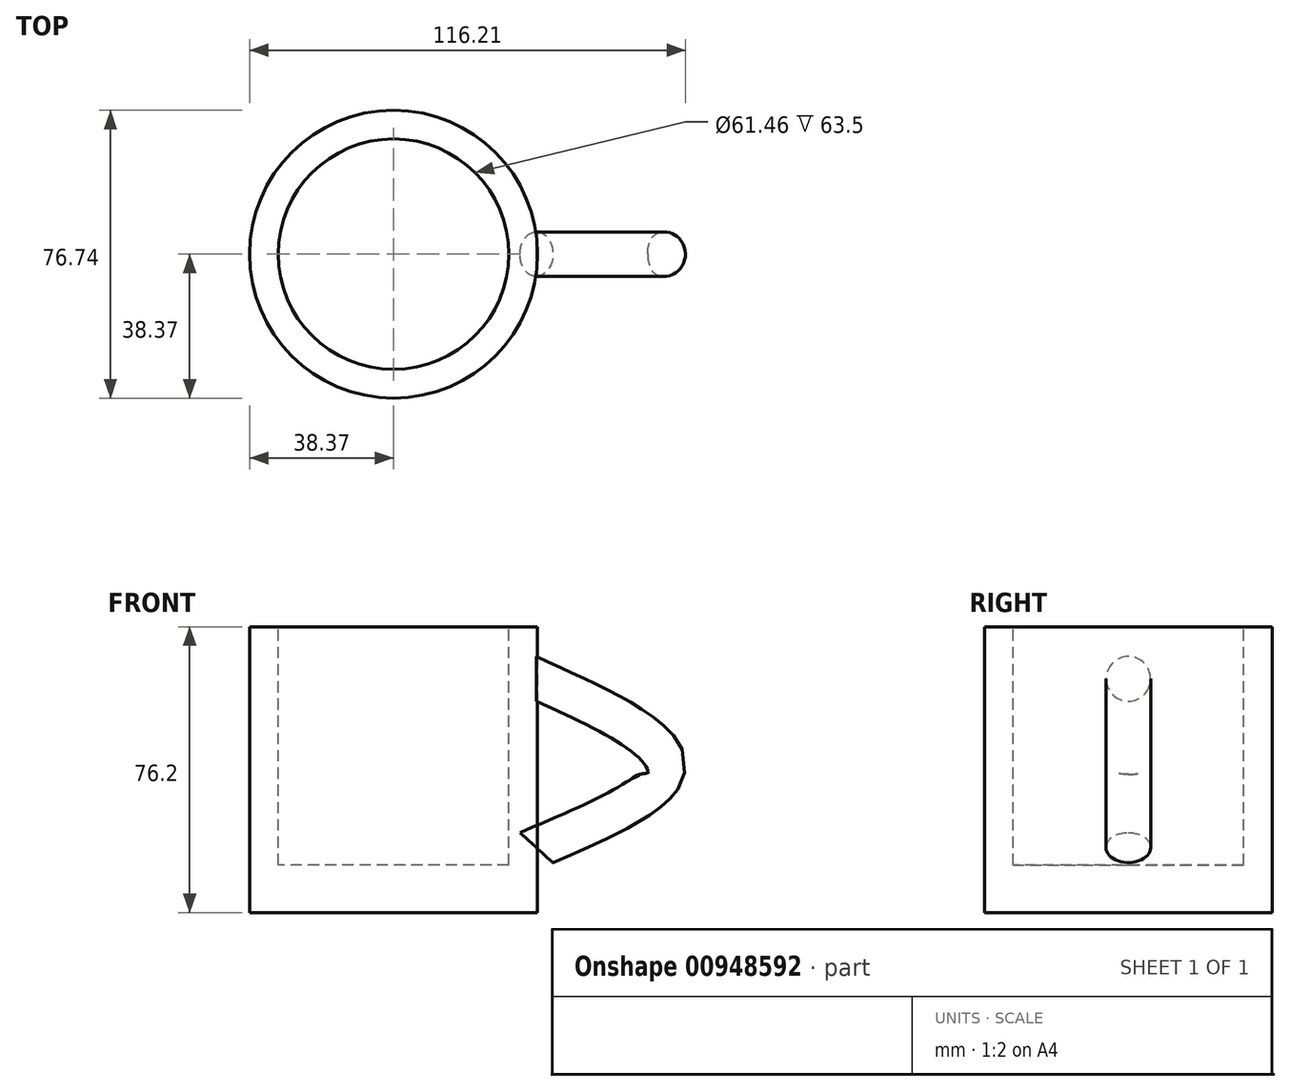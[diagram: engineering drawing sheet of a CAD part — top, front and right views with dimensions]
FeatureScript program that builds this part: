
annotation { "Feature Type Name" : "Feature", "Feature Type Description" : "" }
export const myFeature = defineFeature(function(context is Context, id is Id, definition is map)
    precondition{}
    {
        {
            var Q0;
            Q0=qCreatedBy(makeId("Top.planeOp"),FACE);
            var sketch = newSketch(context, id + "F0", { "sketchPlane" : qUnion([Q0])});
            skCircle(sketch, "E0", {"center": v(0, 0) * mm, "radius": 38.37 * mm});
            skSolve(sketch);
        }
        {
            var Q0;
            Q0=makeQuery(id+"F0.imprint","IMPRINT",FACE,{"disambiguationData":[TD([[makeQuery(id+"F0.imprint","IMPRINT",EDGE,{"derivedFrom":sQuery(id+"F0.wireOp",EDGE,"E0")}),1.0]])]});
            extrude(context, id + "F1", {"entities" : qUnion([Q0]), "depth" : 76.2 * mm, "offsetDistance" : 25.4 * mm});
        }
        {
            var Q0;
            Q0=makeQuery(id+"F1.opExtrude","CAP_FACE",FACE,{"disambiguationData":[OSD([sQuery(id+"F0.wireOp",EDGE,"E0")])],"isStart":false});
            var sketch = newSketch(context, id + "F2", { "sketchPlane" : qUnion([Q0])});
            skCircle(sketch, "E1", {"center": v(0, 0) * mm, "radius": 30.73 * mm});
            skSolve(sketch);
        }
        {
            var Q0;
            Q0=makeQuery(id+"F2.imprint","IMPRINT",FACE,{"disambiguationData":[TD([[makeQuery(id+"F2.imprint","IMPRINT",EDGE,{"derivedFrom":sQuery(id+"F2.wireOp",EDGE,"E1")}),1.0]])]});
            extrude(context, id + "F3", {"entities" : qUnion([Q0]), "operationType" : NewBodyOperationType.REMOVE, "oppositeDirection" : true, "depth" : 63.5 * mm, "offsetDistance" : 25.4 * mm});
        }
        {
            var Q0;
            Q0=qCreatedBy(makeId("Right.planeOp"),FACE);
            var sketch = newSketch(context, id + "F4", { "sketchPlane" : qUnion([Q0])});
            skCircle(sketch, "E2", {"center": v(0, 62.32) * mm, "radius": 5.94 * mm});
            skCircle(sketch, "E3", {"center": v(0, 17.08) * mm, "radius": 6.6 * mm});
            skSolve(sketch);
        }
        {
            var Q0;
            Q0=qCreatedBy(makeId("Front.planeOp"),FACE);
            var sketch = newSketch(context, id + "F5", { "sketchPlane" : qUnion([Q0])});
            skFitSpline(sketch, "E4", {"points": [v(0, 62.32) * mm, v(34.05, 39.22) * mm, v(0, 17.33) * mm], "startDerivative": vector(102.01, -46.53) * mm, "endDerivative": vector(-102.29, -43.47) * mm});
            skSolve(sketch);
        }
        {
            var Q0;
            Q0=makeQuery(id+"F4.imprint","IMPRINT",FACE,{"disambiguationData":[TD([[makeQuery(id+"F4.imprint","IMPRINT",EDGE,{"derivedFrom":sQuery(id+"F4.wireOp",EDGE,"E2")}),1.0]])]});
            var Q1;
            Q1=sQuery(id+"F5.wireOp",EDGE,"E4");
            sweep(context, id + "F6", {"profiles" : qUnion([Q0]), "path" : qUnion([Q1])});
        }
        {
            var Q0;
            Q0=makeQuery(id+"F6.opSweep","SWEPT_BODY",BODY,{"disambiguationData":[OSD([sQuery(id+"F4.wireOp",EDGE,"E2"),sQuery(id+"F5.wireOp",EDGE,"E4")])]});
            transform(context, id + "F7", {"entities" : qUnion([Q0]), "transformType" : TransformType.TRANSLATION_3D, "dx" : 38.1 * mm, "dy" : 0 * mm, "dz" : 0 * mm, "makeCopy" : false});
        }
    });
